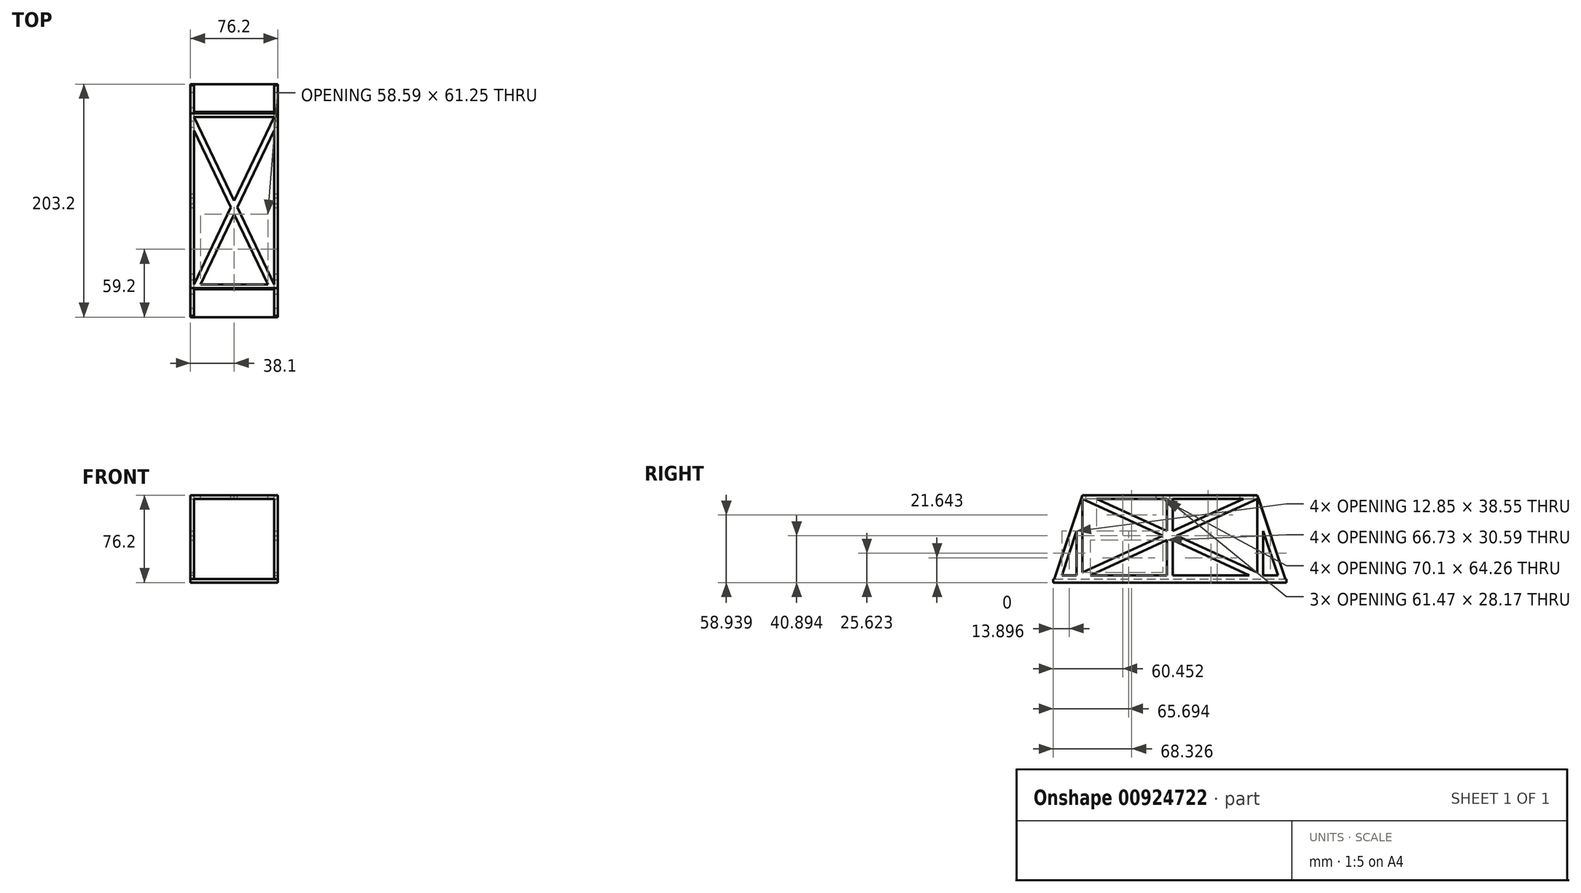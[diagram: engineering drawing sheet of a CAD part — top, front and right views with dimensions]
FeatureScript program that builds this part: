
annotation { "Feature Type Name" : "Feature", "Feature Type Description" : "" }
export const myFeature = defineFeature(function(context is Context, id is Id, definition is map)
    precondition{}
    {
        {
            var Q0;
            Q0=qCreatedBy(makeId("Right.planeOp"),FACE);
            var sketch = newSketch(context, id + "F0", { "sketchPlane" : qUnion([Q0])});
            skLineSegment(sketch, "E0", {"start": v(-101.6, -38.1) * mm, "end": v(101.6, -38.1) * mm});
            skLineSegment(sketch, "E1", {"start": v(-76.2, 38.1) * mm, "end": v(76.2, 38.1) * mm});
            skLineSegment(sketch, "E2", {"start": v(76.2, 38.1) * mm, "end": v(101.6, -38.1) * mm});
            skLineSegment(sketch, "E3", {"start": v(-76.2, 38.1) * mm, "end": v(-101.6, -38.1) * mm});
            skSolve(sketch);
        }
        {
            var Q0;
            Q0=qSketchRegion(id+"F0",true);
            extrude(context, id + "F1", {"entities" : qUnion([Q0]), "endBound" : BoundingType.SYMMETRIC, "depth" : 76.2 * mm, "offsetDistance" : 25.4 * mm});
        }
        {
            var Q0;
            Q0=qCreatedBy(makeId("Front.planeOp"),FACE);
            var sketch = newSketch(context, id + "F2", { "sketchPlane" : qUnion([Q0])});
            skLineSegment(sketch, "E4.bottom", {"start": v(34.93, -34.92) * mm, "end": v(-34.93, -34.92) * mm});
            skLineSegment(sketch, "E4.top", {"start": v(34.93, 34.93) * mm, "end": v(-34.93, 34.92) * mm});
            skLineSegment(sketch, "E4.left", {"start": v(34.93, -34.92) * mm, "end": v(34.93, 34.92) * mm});
            skLineSegment(sketch, "E4.right", {"start": v(-34.93, -34.92) * mm, "end": v(-34.93, 34.92) * mm});
            skPoint(sketch, "E4.middle", {"position": v(0, 0) * mm});
            skSolve(sketch);
        }
        {
            var Q0;
            Q0=qSketchRegion(id+"F2",true);
            extrude(context, id + "F3", {"entities" : qUnion([Q0]), "operationType" : NewBodyOperationType.REMOVE, "endBound" : BoundingType.SYMMETRIC, "depth" : 254 * mm, "offsetDistance" : 25.4 * mm});
        }
        {
            var Q0;
            Q0=makeQuery(id+"F1.opExtrude","CAP_FACE",FACE,{"disambiguationData":[OSD([sQuery(id+"F0.wireOp",EDGE,"E0"),sQuery(id+"F0.wireOp",EDGE,"E1"),sQuery(id+"F0.wireOp",EDGE,"E2"),sQuery(id+"F0.wireOp",EDGE,"E3")])],"isStart":false});
            var sketch = newSketch(context, id + "F4", { "sketchPlane" : qUnion([Q0])});
            skLineSegment(sketch, "E5.bottom", {"start": v(76.2, -34.92) * mm, "end": v(-76.2, -34.92) * mm});
            skLineSegment(sketch, "E5.top", {"start": v(76.2, 34.92) * mm, "end": v(-76.2, 34.92) * mm});
            skLineSegment(sketch, "E5.left", {"start": v(76.2, -34.92) * mm, "end": v(76.2, 34.92) * mm});
            skLineSegment(sketch, "E5.right", {"start": v(-76.2, -34.92) * mm, "end": v(-76.2, 34.92) * mm});
            skPoint(sketch, "E5.middle", {"position": v(0, 0) * mm});
            skLineSegment(sketch, "E6", {"start": v(-81.28, -34.92) * mm, "end": v(-81.28, 6.8) * mm});
            skLineSegment(sketch, "E7", {"start": v(-81.28, 6.8) * mm, "end": v(-95.19, -34.93) * mm});
            skLineSegment(sketch, "E8", {"start": v(-95.19, -34.92) * mm, "end": v(-81.28, -34.92) * mm});
            skLineSegment(sketch, "E9.MirrorCS", {"start": v(81.28, -34.92) * mm, "end": v(81.28, 6.8) * mm});
            skLineSegment(sketch, "E10.MirrorCS", {"start": v(81.28, 6.8) * mm, "end": v(95.19, -34.93) * mm});
            skLineSegment(sketch, "E11.MirrorCS", {"start": v(95.19, -34.92) * mm, "end": v(81.28, -34.92) * mm});
            skLineSegment(sketch, "E12", {"start": v(-76.2, 34.92) * mm, "end": v(76.2, -34.92) * mm});
            skLineSegment(sketch, "E13", {"start": v(76.2, 34.92) * mm, "end": v(-76.2, -34.92) * mm});
            skLineSegment(sketch, "E14", {"start": v(-76.2, -29.34) * mm, "end": v(64, 34.93) * mm});
            skLineSegment(sketch, "E15", {"start": v(76.2, -29.34) * mm, "end": v(-64, 34.92) * mm});
            skLineSegment(sketch, "E16.bottom", {"start": v(2.54, -34.92) * mm, "end": v(-2.54, -34.92) * mm});
            skLineSegment(sketch, "E16.top", {"start": v(2.54, 34.92) * mm, "end": v(-2.54, 34.92) * mm});
            skLineSegment(sketch, "E16.left", {"start": v(2.54, -34.93) * mm, "end": v(2.54, 34.93) * mm});
            skLineSegment(sketch, "E16.right", {"start": v(-2.54, -34.93) * mm, "end": v(-2.54, 34.93) * mm});
            skSolve(sketch);
        }
        {
            var Q0;
            Q0=makeQuery(id+"F4.imprint","IMPRINT",FACE,{"disambiguationData":[TD([[makeQuery(id+"F4.imprint","IMPRINT",EDGE,{"derivedFrom":sQuery(id+"F4.wireOp",EDGE,"E6")}),1.0]])]});
            var Q1;
            {var subQ1=sQuery(id+"F4.wireOp",EDGE,"E5.right");var subQ3=sQuery(id+"F4.wireOp",EDGE,"E14");var subQ4=makeQuery(id+"F4.imprint","INTERSECT",VERTEX,{"derivedFrom":[subQ1,subQ3]});Q1=makeQuery(id+"F4.imprint","IMPRINT",FACE,{"disambiguationData":[TD([[makeQuery(id+"F4.imprint","IMPRINT",EDGE,{"disambiguationData":[TD([[subQ4,-1.0]])],"derivedFrom":subQ3}),1.0]])]});}
            var Q2;
            {var subQ0=sQuery(id+"F4.wireOp",EDGE,"E15");var subQ1=sQuery(id+"F4.wireOp",EDGE,"E5.top");var subQ2=makeQuery(id+"F4.imprint","INTERSECT",VERTEX,{"derivedFrom":[subQ1,subQ0]});Q2=makeQuery(id+"F4.imprint","IMPRINT",FACE,{"disambiguationData":[TD([[makeQuery(id+"F4.imprint","IMPRINT",EDGE,{"disambiguationData":[TD([[subQ2,1.0]])],"derivedFrom":subQ0}),-1.0]])]});}
            var Q3;
            {var subQ0=sQuery(id+"F4.wireOp",EDGE,"E14");var subQ1=sQuery(id+"F4.wireOp",EDGE,"E5.top");var subQ2=makeQuery(id+"F4.imprint","INTERSECT",VERTEX,{"derivedFrom":[subQ1,subQ0]});Q3=makeQuery(id+"F4.imprint","IMPRINT",FACE,{"disambiguationData":[TD([[makeQuery(id+"F4.imprint","IMPRINT",EDGE,{"disambiguationData":[TD([[subQ2,1.0]])],"derivedFrom":subQ0}),1.0]])]});}
            var Q4;
            {var subQ1=sQuery(id+"F4.wireOp",EDGE,"E5.left");var subQ3=sQuery(id+"F4.wireOp",EDGE,"E15");var subQ4=makeQuery(id+"F4.imprint","INTERSECT",VERTEX,{"derivedFrom":[subQ1,subQ3]});Q4=makeQuery(id+"F4.imprint","IMPRINT",FACE,{"disambiguationData":[TD([[makeQuery(id+"F4.imprint","IMPRINT",EDGE,{"disambiguationData":[TD([[subQ4,-1.0]])],"derivedFrom":subQ3}),-1.0]])]});}
            var Q5;
            Q5=makeQuery(id+"F4.imprint","IMPRINT",FACE,{"disambiguationData":[TD([[makeQuery(id+"F4.imprint","IMPRINT",EDGE,{"derivedFrom":sQuery(id+"F4.wireOp",EDGE,"E9.MirrorCS")}),-1.0]])]});
            var Q6;
            {var subQ0=sQuery(id+"F4.wireOp",EDGE,"E12");var subQ3=sQuery(id+"F4.wireOp",EDGE,"E16.left");var subQ5=makeQuery(id+"F4.imprint","INTERSECT",VERTEX,{"derivedFrom":[subQ0,subQ3]});Q6=makeQuery(id+"F4.imprint","IMPRINT",FACE,{"disambiguationData":[TD([[makeQuery(id+"F4.imprint","IMPRINT",EDGE,{"disambiguationData":[TD([[subQ5,-1.0]])],"derivedFrom":subQ0}),-1.0]])]});}
            var Q7;
            {var subQ0=sQuery(id+"F4.wireOp",EDGE,"E13");var subQ3=sQuery(id+"F4.wireOp",EDGE,"E16.right");var subQ5=makeQuery(id+"F4.imprint","INTERSECT",VERTEX,{"derivedFrom":[subQ0,subQ3]});Q7=makeQuery(id+"F4.imprint","IMPRINT",FACE,{"disambiguationData":[TD([[makeQuery(id+"F4.imprint","IMPRINT",EDGE,{"disambiguationData":[TD([[subQ5,-1.0]])],"derivedFrom":subQ0}),1.0]])]});}
            extrude(context, id + "F5", {"entities" : qUnion([Q0, Q1, Q2, Q3, Q4, Q5, Q6, Q7]), "operationType" : NewBodyOperationType.REMOVE, "oppositeDirection" : true, "depth" : 76.2 * mm, "offsetDistance" : 25.4 * mm});
        }
        {
            var Q0;
            Q0=makeQuery(id+"F1.opExtrude","SWEPT_FACE",FACE,{"disambiguationData":[OSD([sQuery(id+"F0.wireOp",EDGE,"E1")])]});
            var sketch = newSketch(context, id + "F6", { "sketchPlane" : qUnion([Q0])});
            skLineSegment(sketch, "E17.bottom", {"start": v(34.93, 73.03) * mm, "end": v(-34.93, 73.03) * mm});
            skLineSegment(sketch, "E17.top", {"start": v(34.93, -73.03) * mm, "end": v(-34.93, -73.03) * mm});
            skLineSegment(sketch, "E17.left", {"start": v(34.93, -73.03) * mm, "end": v(34.93, 73.03) * mm});
            skLineSegment(sketch, "E17.right", {"start": v(-34.93, -73.03) * mm, "end": v(-34.93, 73.03) * mm});
            skPoint(sketch, "E17.middle", {"position": v(0, 0) * mm});
            skLineSegment(sketch, "E18", {"start": v(-34.92, 73.02) * mm, "end": v(34.92, -73.02) * mm});
            skLineSegment(sketch, "E19", {"start": v(34.92, 73.02) * mm, "end": v(-34.92, -73.02) * mm});
            skLineSegment(sketch, "E20", {"start": v(-34.93, 61.25) * mm, "end": v(29.3, -73.03) * mm});
            skLineSegment(sketch, "E21", {"start": v(34.93, 61.25) * mm, "end": v(-29.3, -73.03) * mm});
            skSolve(sketch);
        }
        {
            var Q0;
            {var subQ1=sQuery(id+"F6.wireOp",EDGE,"E17.right");var subQ3=sQuery(id+"F6.wireOp",EDGE,"E20");var subQ4=makeQuery(id+"F6.imprint","INTERSECT",VERTEX,{"derivedFrom":[subQ1,subQ3]});Q0=makeQuery(id+"F6.imprint","IMPRINT",FACE,{"disambiguationData":[TD([[makeQuery(id+"F6.imprint","IMPRINT",EDGE,{"disambiguationData":[TD([[subQ4,-1.0]])],"derivedFrom":subQ3}),-1.0]])]});}
            var Q1;
            {var subQ0=sQuery(id+"F6.wireOp",EDGE,"E17.bottom");Q1=makeQuery(id+"F6.imprint","IMPRINT",FACE,{"disambiguationData":[TD([[makeQuery(id+"F6.imprint","IMPRINT",EDGE,{"derivedFrom":subQ0}),1.0]])]});}
            var Q2;
            {var subQ1=sQuery(id+"F6.wireOp",EDGE,"E17.left");var subQ3=sQuery(id+"F6.wireOp",EDGE,"E21");var subQ4=makeQuery(id+"F6.imprint","INTERSECT",VERTEX,{"derivedFrom":[subQ1,subQ3]});Q2=makeQuery(id+"F6.imprint","IMPRINT",FACE,{"disambiguationData":[TD([[makeQuery(id+"F6.imprint","IMPRINT",EDGE,{"disambiguationData":[TD([[subQ4,-1.0]])],"derivedFrom":subQ3}),1.0]])]});}
            var Q3;
            {var subQ0=sQuery(id+"F6.wireOp",EDGE,"E20");var subQ1=sQuery(id+"F6.wireOp",EDGE,"E17.top");var subQ2=makeQuery(id+"F6.imprint","INTERSECT",VERTEX,{"derivedFrom":[subQ1,subQ0]});Q3=makeQuery(id+"F6.imprint","IMPRINT",FACE,{"disambiguationData":[TD([[makeQuery(id+"F6.imprint","IMPRINT",EDGE,{"disambiguationData":[TD([[subQ2,-1.0]])],"derivedFrom":subQ1}),-1.0]])]});}
            extrude(context, id + "F7", {"entities" : qUnion([Q0, Q1, Q2, Q3]), "operationType" : NewBodyOperationType.REMOVE, "oppositeDirection" : true, "depth" : 3.17 * mm, "offsetDistance" : 25.4 * mm});
        }
        {
            var Q0;
            Q0=makeQuery(id+"F1.opExtrude","CAP_FACE",FACE,{"disambiguationData":[OSD([sQuery(id+"F0.wireOp",EDGE,"E0"),sQuery(id+"F0.wireOp",EDGE,"E1"),sQuery(id+"F0.wireOp",EDGE,"E2"),sQuery(id+"F0.wireOp",EDGE,"E3")])],"isStart":false});
            var sketch = newSketch(context, id + "F8", { "sketchPlane" : qUnion([Q0])});
            skLineSegment(sketch, "E22.bottom", {"start": v(-101.6, -38.1) * mm, "end": v(-95.19, -38.1) * mm});
            skLineSegment(sketch, "E22.top", {"start": v(-101.6, -34.93) * mm, "end": v(-95.19, -34.93) * mm});
            skLineSegment(sketch, "E22.left", {"start": v(-101.6, -38.1) * mm, "end": v(-101.6, -34.93) * mm});
            skLineSegment(sketch, "E22.right", {"start": v(-95.19, -38.1) * mm, "end": v(-95.19, -34.93) * mm});
            skLineSegment(sketch, "E23.MirrorCS", {"start": v(101.6, -38.1) * mm, "end": v(101.6, -34.93) * mm});
            skLineSegment(sketch, "E24.MirrorCS", {"start": v(95.19, -38.1) * mm, "end": v(95.19, -34.93) * mm});
            skLineSegment(sketch, "E25.MirrorCS", {"start": v(101.6, -34.93) * mm, "end": v(95.19, -34.93) * mm});
            skLineSegment(sketch, "E26.MirrorCS", {"start": v(101.6, -38.1) * mm, "end": v(95.19, -38.1) * mm});
            skSolve(sketch);
        }
        {
            var Q0;
            Q0=qSketchRegion(id+"F8",true);
            extrude(context, id + "F9", {"entities" : qUnion([Q0]), "operationType" : NewBodyOperationType.ADD, "oppositeDirection" : true, "depth" : 76.2 * mm, "offsetDistance" : 25.4 * mm});
        }
        {
            var Q0;
            {var subQ0=sQuery(id+"F4.wireOp",EDGE,"E5.bottom");Q0=makeQuery(id+"F9.boolean.opBoolean","MERGE",FACE,{"derivedFrom":[makeQuery(id+"F5.boolean.opBoolean","MERGE",FACE,{"derivedFrom":[makeQuery(id+"F3.boolean.opBoolean","COPY",FACE,{"derivedFrom":makeQuery(id+"F3.opExtrude","SWEPT_FACE",FACE,{"disambiguationData":[OSD([sQuery(id+"F2.wireOp",EDGE,"E4.bottom")])]})})],"fromTools":[makeQuery(id+"F5.opExtrude","SWEPT_FACE",FACE,{"disambiguationData":[OSD([subQ0]),TDD([makeQuery(id+"F4.imprint","IMPRINT",EDGE,{"disambiguationData":[TD([[makeQuery(id+"F4.imprint","INTERSECT",VERTEX,{"derivedFrom":[subQ0,sQuery(id+"F4.wireOp",EDGE,"E5.left"),sQuery(id+"F4.wireOp",EDGE,"E12")]}),-1.0]])],"derivedFrom":subQ0})])]}),makeQuery(id+"F5.opExtrude","SWEPT_FACE",FACE,{"disambiguationData":[OSD([subQ0]),TDD([makeQuery(id+"F4.imprint","IMPRINT",EDGE,{"disambiguationData":[TD([[makeQuery(id+"F4.imprint","INTERSECT",VERTEX,{"derivedFrom":[subQ0,sQuery(id+"F4.wireOp",EDGE,"E5.right"),sQuery(id+"F4.wireOp",EDGE,"E13")]}),1.0]])],"derivedFrom":subQ0})])]}),makeQuery(id+"F5.opExtrude","SWEPT_FACE",FACE,{"disambiguationData":[OSD([sQuery(id+"F4.wireOp",EDGE,"E8")])]}),makeQuery(id+"F5.opExtrude","SWEPT_FACE",FACE,{"disambiguationData":[OSD([sQuery(id+"F4.wireOp",EDGE,"E11.MirrorCS")])]})]}),makeQuery(id+"F9.opExtrude","SWEPT_FACE",FACE,{"disambiguationData":[OSD([sQuery(id+"F8.wireOp",EDGE,"E22.top")])]}),makeQuery(id+"F9.opExtrude","SWEPT_FACE",FACE,{"disambiguationData":[OSD([sQuery(id+"F8.wireOp",EDGE,"E25.MirrorCS")])]})]});}
            var sketch = newSketch(context, id + "F10", { "sketchPlane" : qUnion([Q0])});
            skLineSegment(sketch, "E27.bottom", {"start": v(38.1, -95.19) * mm, "end": v(34.92, -95.19) * mm});
            skLineSegment(sketch, "E27.top", {"start": v(38.1, 95.19) * mm, "end": v(34.92, 95.19) * mm});
            skLineSegment(sketch, "E27.left", {"start": v(38.1, -95.19) * mm, "end": v(38.1, 95.19) * mm});
            skLineSegment(sketch, "E27.right", {"start": v(34.92, -95.19) * mm, "end": v(34.92, 95.19) * mm});
            skLineSegment(sketch, "E28.MirrorCS", {"start": v(-34.92, -95.19) * mm, "end": v(-34.92, 95.19) * mm});
            skLineSegment(sketch, "E29.MirrorCS", {"start": v(-38.1, -95.19) * mm, "end": v(-38.1, 95.19) * mm});
            skLineSegment(sketch, "E30.MirrorCS", {"start": v(-38.1, -95.19) * mm, "end": v(-34.92, -95.19) * mm});
            skLineSegment(sketch, "E31.MirrorCS", {"start": v(-38.1, 95.19) * mm, "end": v(-34.92, 95.19) * mm});
            skSolve(sketch);
        }
        {
            var Q0;
            Q0=qSketchRegion(id+"F10",true);
            extrude(context, id + "F11", {"entities" : qUnion([Q0]), "operationType" : NewBodyOperationType.ADD, "depth" : 3.17 * mm, "offsetDistance" : 25.4 * mm});
        }
    });
